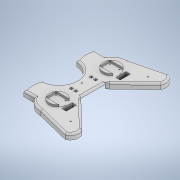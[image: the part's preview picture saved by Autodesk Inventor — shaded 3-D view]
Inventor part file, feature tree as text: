
AUTODESK INVENTOR PART (.ipt)
format: ipt  version: 2021 (Build 250183000, 183)  size: 361,984 bytes
history: native  units: mm
features: extrude x8, sketch x8, other x1, fillet x1
ambient origin geometry x8: Origin, YZ Plane, XZ Plane, XY Plane, X Axis, Y Axis, Z Axis, Center Point
bodies: Body1 (feature_tree)
feature tree (18):
  other  "Sólido1"
  extrude  "Extrusión1"  Depth=10.0mm TaperAngle=0.0deg
  extrude  "Extrusión2"  Depth=5.0mm TaperAngle=0.0deg
  extrude  "Extrusión3"  Depth=5.0mm
  extrude  "Extrusión4"  Depth=12.0mm TaperAngle=0.0deg
  extrude  "Extrusión5"  Depth=10.0mm TaperAngle=0.0deg
  fillet  "Empalme1"  Radius=0.5mm
  extrude  "Extrusión6"  [1 undecoded]
  extrude  "Extrusión7"  [1 undecoded]
  extrude  "Extrusión8"  [1 undecoded]
  sketch  "Boceto1"  dims[d21=5.0mm d22=0.0mm d25=10.0mm d26=0.0mm]
  sketch  "Boceto2"  dims[d27=5.0mm d28=0.0mm d29=5.0mm d30=0.0mm]
  sketch  "Boceto3"  dims[d41=15.0mm d42=0.0mm d43=5.0mm]
  sketch  "Boceto4"  dims[d45=12.0mm d46=15.0mm d47=0.0mm]
  sketch  "Boceto5"  dims[d53=16.0mm d54=0.0mm d64=10.0mm d65=0.0mm d55=0.5mm]
  sketch  "Boceto6"  dims[d56=0.872665mm]
  sketch  "Boceto7"
  sketch  "Boceto8"
note: 3 required parameter values undecoded (feature->parameter linkage not recoverable at this tier; creation-order binding heuristic only, values carry confidence <= 0.55)
